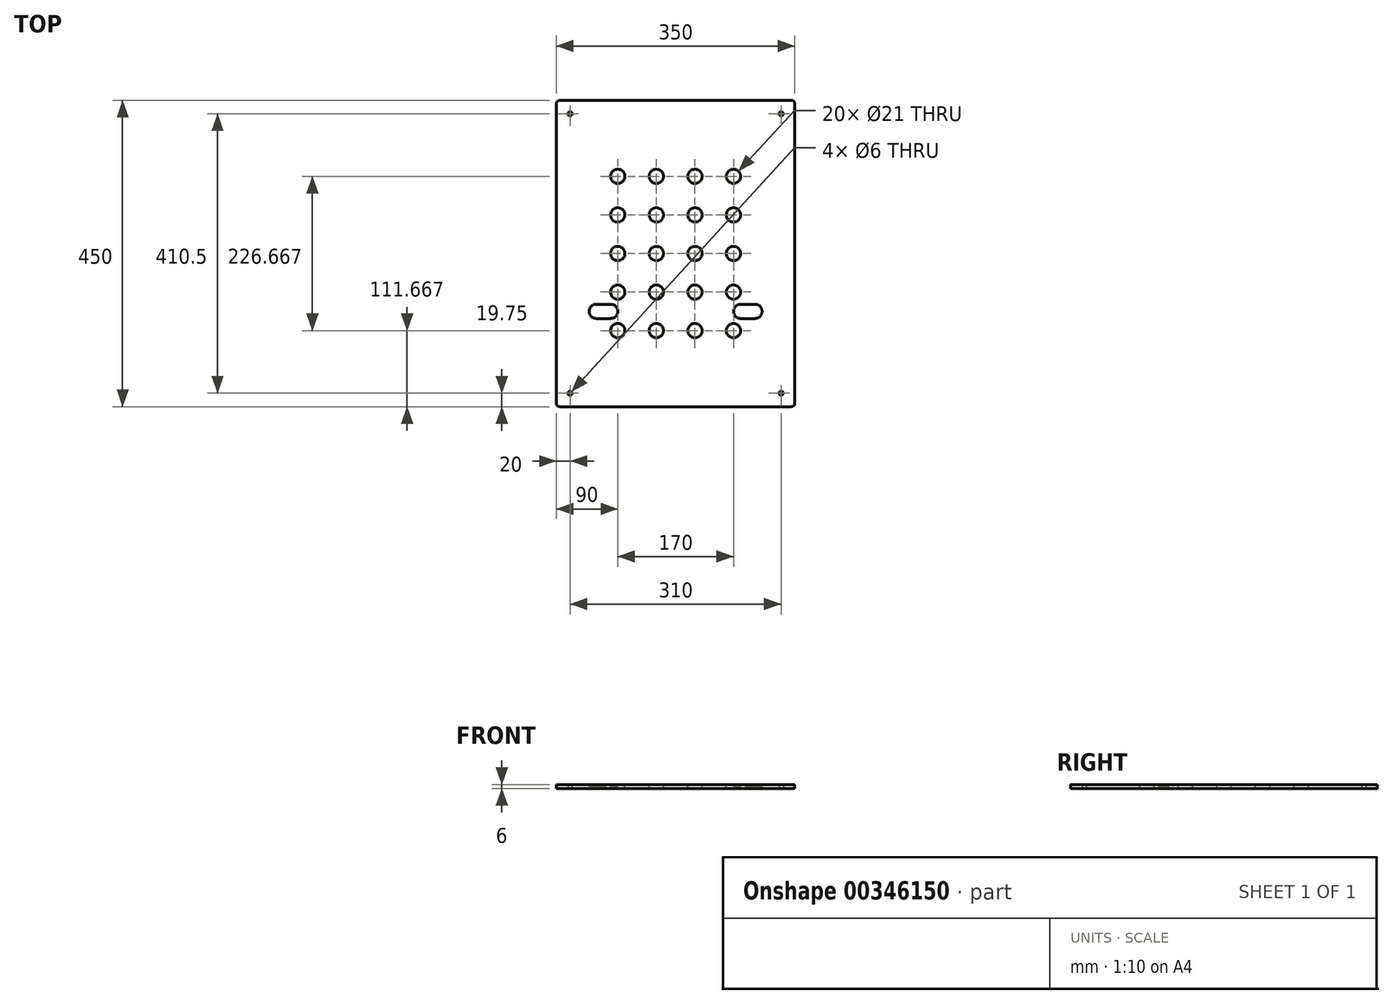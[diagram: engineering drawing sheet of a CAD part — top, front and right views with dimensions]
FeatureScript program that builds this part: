
annotation { "Feature Type Name" : "Feature", "Feature Type Description" : "" }
export const myFeature = defineFeature(function(context is Context, id is Id, definition is map)
    precondition{}
    {
        {
            var Q0;
            Q0=qCreatedBy(makeId("Top.planeOp"),FACE);
            var sketch = newSketch(context, id + "F0", { "sketchPlane" : qUnion([Q0])});
            skLineSegment(sketch, "E0.bottom", {"start": v(-170, 225) * mm, "end": v(170, 225) * mm});
            skLineSegment(sketch, "E0.top", {"start": v(-170, -225) * mm, "end": v(170, -225) * mm});
            skLineSegment(sketch, "E0.left", {"start": v(-175, 220) * mm, "end": v(-175, -220) * mm});
            skLineSegment(sketch, "E0.right", {"start": v(175, 220) * mm, "end": v(175, -220) * mm});
            skCircle(sketch, "E1", {"center": v(155, 205.25) * mm, "radius": 3 * mm});
            skCircle(sketch, "E2", {"center": v(155, -205.25) * mm, "radius": 3 * mm});
            skCircle(sketch, "E3", {"center": v(-155, -205.25) * mm, "radius": 3 * mm});
            skCircle(sketch, "E4", {"center": v(-155, 205.25) * mm, "radius": 3 * mm});
            skPoint(sketch, "E5.visualSharp", {"position": v(-175, 225) * mm});
            skArc(sketch, "E5.filletArc", {"start": v(-170, 225) * mm, "mid": v(-173.54, 223.54) * mm, "end": v(-175, 220) * mm});
            skPoint(sketch, "E6.visualSharp", {"position": v(-175, -225) * mm});
            skArc(sketch, "E6.filletArc", {"start": v(-175, -220) * mm, "mid": v(-173.54, -223.54) * mm, "end": v(-170, -225) * mm});
            skPoint(sketch, "E7.visualSharp", {"position": v(175, -225) * mm});
            skArc(sketch, "E7.filletArc", {"start": v(170, -225) * mm, "mid": v(173.54, -223.54) * mm, "end": v(175, -220) * mm});
            skPoint(sketch, "E8.visualSharp", {"position": v(175, 225) * mm});
            skArc(sketch, "E8.filletArc", {"start": v(175, 220) * mm, "mid": v(173.54, 223.54) * mm, "end": v(170, 225) * mm});
            skSolve(sketch);
        }
        {
            var Q0;
            Q0=makeQuery(id+"F0.imprint","IMPRINT",FACE,{"disambiguationData":[TD([[makeQuery(id+"F0.imprint","IMPRINT",EDGE,{"derivedFrom":sQuery(id+"F0.wireOp",EDGE,"E0.bottom")}),-1.0]])]});
            extrude(context, id + "F1", {"entities" : qUnion([Q0]), "depth" : 6 * mm});
        }
        {
            var Q0;
            Q0=makeQuery(id+"F1.opExtrude","CAP_FACE",FACE,{"disambiguationData":[OSD([sQuery(id+"F0.wireOp",EDGE,"E0.bottom"),sQuery(id+"F0.wireOp",EDGE,"E0.top"),sQuery(id+"F0.wireOp",EDGE,"E0.left"),sQuery(id+"F0.wireOp",EDGE,"E0.right"),sQuery(id+"F0.wireOp",EDGE,"E1"),sQuery(id+"F0.wireOp",EDGE,"E2"),sQuery(id+"F0.wireOp",EDGE,"E3"),sQuery(id+"F0.wireOp",EDGE,"E4"),sQuery(id+"F0.wireOp",EDGE,"E5.filletArc"),sQuery(id+"F0.wireOp",EDGE,"E6.filletArc"),sQuery(id+"F0.wireOp",EDGE,"E7.filletArc"),sQuery(id+"F0.wireOp",EDGE,"E8.filletArc")])],"isStart":false});
            var sketch = newSketch(context, id + "F2", { "sketchPlane" : qUnion([Q0])});
            skLineSegment(sketch, "E9.bottom", {"start": v(-125, 145) * mm, "end": v(125, 145) * mm, "construction": true});
            skLineSegment(sketch, "E9.top", {"start": v(-125, -145) * mm, "end": v(125, -145) * mm, "construction": true});
            skLineSegment(sketch, "E9.left", {"start": v(-125, 145) * mm, "end": v(-125, -145) * mm, "construction": true});
            skLineSegment(sketch, "E9.right", {"start": v(125, 145) * mm, "end": v(125, -145) * mm, "construction": true});
            skCircle(sketch, "E10", {"center": v(-85, 113.33) * mm, "radius": 10.5 * mm});
            skCircle(sketch, "E11.0.1.0", {"center": v(-85, 56.67) * mm, "radius": 10.5 * mm});
            skCircle(sketch, "E11.0.2.0", {"center": v(-85, 0) * mm, "radius": 10.5 * mm});
            skCircle(sketch, "E11.1.0.0", {"center": v(-28.33, 113.33) * mm, "radius": 10.5 * mm});
            skCircle(sketch, "E11.1.1.0", {"center": v(-28.33, 56.67) * mm, "radius": 10.5 * mm});
            skCircle(sketch, "E11.1.2.0", {"center": v(-28.33, 0) * mm, "radius": 10.5 * mm});
            skCircle(sketch, "E11.2.0.0", {"center": v(28.33, 113.33) * mm, "radius": 10.5 * mm});
            skCircle(sketch, "E11.2.1.0", {"center": v(28.33, 56.67) * mm, "radius": 10.5 * mm});
            skCircle(sketch, "E11.2.2.0", {"center": v(28.33, 0) * mm, "radius": 10.5 * mm});
            skLineSegment(sketch, "E11.direction1", {"start": v(-85, 113.33) * mm, "end": v(-28.33, 113.33) * mm, "construction": true});
            skLineSegment(sketch, "E11.direction2", {"start": v(-85, 113.33) * mm, "end": v(-85, 56.67) * mm, "construction": true});
            skCircle(sketch, "E12.0.0.3", {"center": v(-85, -56.67) * mm, "radius": 10.5 * mm});
            skCircle(sketch, "E12.0.0.4", {"center": v(-85, -113.33) * mm, "radius": 10.5 * mm});
            skCircle(sketch, "E12.0.1.3", {"center": v(-28.33, -56.67) * mm, "radius": 10.5 * mm});
            skCircle(sketch, "E12.0.1.4", {"center": v(-28.33, -113.33) * mm, "radius": 10.5 * mm});
            skCircle(sketch, "E12.0.2.3", {"center": v(28.33, -56.67) * mm, "radius": 10.5 * mm});
            skCircle(sketch, "E12.0.2.4", {"center": v(28.33, -113.33) * mm, "radius": 10.5 * mm});
            skCircle(sketch, "E13.0.3.0", {"center": v(85, 113.33) * mm, "radius": 10.5 * mm});
            skCircle(sketch, "E13.0.3.1", {"center": v(85, 56.67) * mm, "radius": 10.5 * mm});
            skCircle(sketch, "E13.0.3.2", {"center": v(85, 0) * mm, "radius": 10.5 * mm});
            skCircle(sketch, "E13.0.3.3", {"center": v(85, -56.67) * mm, "radius": 10.5 * mm});
            skCircle(sketch, "E13.0.3.4", {"center": v(85, -113.33) * mm, "radius": 10.5 * mm});
            skSolve(sketch);
        }
        {
            var Q0;
            Q0=makeQuery(id+"F2.imprint","IMPRINT",FACE,{"disambiguationData":[TD([[makeQuery(id+"F2.imprint","IMPRINT",EDGE,{"derivedFrom":sQuery(id+"F2.wireOp",EDGE,"E10")}),1.0]])]});
            var Q1;
            Q1=makeQuery(id+"F2.imprint","IMPRINT",FACE,{"disambiguationData":[TD([[makeQuery(id+"F2.imprint","IMPRINT",EDGE,{"derivedFrom":sQuery(id+"F2.wireOp",EDGE,"E11.0.1.0")}),1.0]])]});
            var Q2;
            Q2=makeQuery(id+"F2.imprint","IMPRINT",FACE,{"disambiguationData":[TD([[makeQuery(id+"F2.imprint","IMPRINT",EDGE,{"derivedFrom":sQuery(id+"F2.wireOp",EDGE,"E11.0.2.0")}),1.0]])]});
            var Q3;
            Q3=makeQuery(id+"F2.imprint","IMPRINT",FACE,{"disambiguationData":[TD([[makeQuery(id+"F2.imprint","IMPRINT",EDGE,{"derivedFrom":sQuery(id+"F2.wireOp",EDGE,"E12.0.0.3")}),1.0]])]});
            var Q4;
            Q4=makeQuery(id+"F2.imprint","IMPRINT",FACE,{"disambiguationData":[TD([[makeQuery(id+"F2.imprint","IMPRINT",EDGE,{"derivedFrom":sQuery(id+"F2.wireOp",EDGE,"E12.0.0.4")}),1.0]])]});
            var Q5;
            Q5=makeQuery(id+"F2.imprint","IMPRINT",FACE,{"disambiguationData":[TD([[makeQuery(id+"F2.imprint","IMPRINT",EDGE,{"derivedFrom":sQuery(id+"F2.wireOp",EDGE,"E12.0.1.4")}),1.0]])]});
            var Q6;
            Q6=makeQuery(id+"F2.imprint","IMPRINT",FACE,{"disambiguationData":[TD([[makeQuery(id+"F2.imprint","IMPRINT",EDGE,{"derivedFrom":sQuery(id+"F2.wireOp",EDGE,"E12.0.1.3")}),1.0]])]});
            var Q7;
            Q7=makeQuery(id+"F2.imprint","IMPRINT",FACE,{"disambiguationData":[TD([[makeQuery(id+"F2.imprint","IMPRINT",EDGE,{"derivedFrom":sQuery(id+"F2.wireOp",EDGE,"E11.1.2.0")}),1.0]])]});
            var Q8;
            Q8=makeQuery(id+"F2.imprint","IMPRINT",FACE,{"disambiguationData":[TD([[makeQuery(id+"F2.imprint","IMPRINT",EDGE,{"derivedFrom":sQuery(id+"F2.wireOp",EDGE,"E11.1.1.0")}),1.0]])]});
            var Q9;
            Q9=makeQuery(id+"F2.imprint","IMPRINT",FACE,{"disambiguationData":[TD([[makeQuery(id+"F2.imprint","IMPRINT",EDGE,{"derivedFrom":sQuery(id+"F2.wireOp",EDGE,"E11.1.0.0")}),1.0]])]});
            var Q10;
            Q10=makeQuery(id+"F2.imprint","IMPRINT",FACE,{"disambiguationData":[TD([[makeQuery(id+"F2.imprint","IMPRINT",EDGE,{"derivedFrom":sQuery(id+"F2.wireOp",EDGE,"E11.2.0.0")}),1.0]])]});
            var Q11;
            Q11=makeQuery(id+"F2.imprint","IMPRINT",FACE,{"disambiguationData":[TD([[makeQuery(id+"F2.imprint","IMPRINT",EDGE,{"derivedFrom":sQuery(id+"F2.wireOp",EDGE,"E11.2.1.0")}),1.0]])]});
            var Q12;
            Q12=makeQuery(id+"F2.imprint","IMPRINT",FACE,{"disambiguationData":[TD([[makeQuery(id+"F2.imprint","IMPRINT",EDGE,{"derivedFrom":sQuery(id+"F2.wireOp",EDGE,"E11.2.2.0")}),1.0]])]});
            var Q13;
            Q13=makeQuery(id+"F2.imprint","IMPRINT",FACE,{"disambiguationData":[TD([[makeQuery(id+"F2.imprint","IMPRINT",EDGE,{"derivedFrom":sQuery(id+"F2.wireOp",EDGE,"E12.0.2.3")}),1.0]])]});
            var Q14;
            Q14=makeQuery(id+"F2.imprint","IMPRINT",FACE,{"disambiguationData":[TD([[makeQuery(id+"F2.imprint","IMPRINT",EDGE,{"derivedFrom":sQuery(id+"F2.wireOp",EDGE,"E12.0.2.4")}),1.0]])]});
            var Q15;
            Q15=makeQuery(id+"F2.imprint","IMPRINT",FACE,{"disambiguationData":[TD([[makeQuery(id+"F2.imprint","IMPRINT",EDGE,{"derivedFrom":sQuery(id+"F2.wireOp",EDGE,"E13.0.3.4")}),1.0]])]});
            var Q16;
            Q16=makeQuery(id+"F2.imprint","IMPRINT",FACE,{"disambiguationData":[TD([[makeQuery(id+"F2.imprint","IMPRINT",EDGE,{"derivedFrom":sQuery(id+"F2.wireOp",EDGE,"E13.0.3.3")}),1.0]])]});
            var Q17;
            Q17=makeQuery(id+"F2.imprint","IMPRINT",FACE,{"disambiguationData":[TD([[makeQuery(id+"F2.imprint","IMPRINT",EDGE,{"derivedFrom":sQuery(id+"F2.wireOp",EDGE,"E13.0.3.2")}),1.0]])]});
            var Q18;
            Q18=makeQuery(id+"F2.imprint","IMPRINT",FACE,{"disambiguationData":[TD([[makeQuery(id+"F2.imprint","IMPRINT",EDGE,{"derivedFrom":sQuery(id+"F2.wireOp",EDGE,"E13.0.3.1")}),1.0]])]});
            var Q19;
            Q19=makeQuery(id+"F2.imprint","IMPRINT",FACE,{"disambiguationData":[TD([[makeQuery(id+"F2.imprint","IMPRINT",EDGE,{"derivedFrom":sQuery(id+"F2.wireOp",EDGE,"E13.0.3.0")}),1.0]])]});
            extrude(context, id + "F3", {"entities" : qUnion([Q0, Q1, Q2, Q3, Q4, Q5, Q6, Q7, Q8, Q9, Q10, Q11, Q12, Q13, Q14, Q15, Q16, Q17, Q18, Q19]), "operationType" : NewBodyOperationType.REMOVE, "oppositeDirection" : true, "depth" : 25 * mm});
        }
        {
            var Q0;
            Q0=makeQuery(id+"F1.opExtrude","CAP_FACE",FACE,{"disambiguationData":[OSD([sQuery(id+"F0.wireOp",EDGE,"E0.bottom"),sQuery(id+"F0.wireOp",EDGE,"E0.top"),sQuery(id+"F0.wireOp",EDGE,"E0.left"),sQuery(id+"F0.wireOp",EDGE,"E0.right"),sQuery(id+"F0.wireOp",EDGE,"E1"),sQuery(id+"F0.wireOp",EDGE,"E2"),sQuery(id+"F0.wireOp",EDGE,"E3"),sQuery(id+"F0.wireOp",EDGE,"E4"),sQuery(id+"F0.wireOp",EDGE,"E5.filletArc"),sQuery(id+"F0.wireOp",EDGE,"E6.filletArc"),sQuery(id+"F0.wireOp",EDGE,"E7.filletArc"),sQuery(id+"F0.wireOp",EDGE,"E8.filletArc")])],"isStart":false});
            var sketch = newSketch(context, id + "F4", { "sketchPlane" : qUnion([Q0])});
            skPoint(sketch, "E14.startSnap0", {"position": v(-85, 28.33) * mm});
            skLineSegment(sketch, "E15", {"start": v(-85, -56.67) * mm, "end": v(-85, -113.33) * mm, "construction": true});
            skLineSegment(sketch, "E16", {"start": v(85, -56.67) * mm, "end": v(85, -113.33) * mm, "construction": true});
            skLineSegment(sketch, "E17", {"start": v(85, -85) * mm, "end": v(-85, -85) * mm, "construction": true});
            skLineSegment(sketch, "E18.bottom", {"start": v(-116.5, -74.5) * mm, "end": v(-95.5, -74.5) * mm});
            skLineSegment(sketch, "E18.top", {"start": v(-116.5, -95.5) * mm, "end": v(-95.5, -95.5) * mm});
            skLineSegment(sketch, "E18.left", {"start": v(-116.5, -74.5) * mm, "end": v(-116.5, -95.5) * mm, "construction": true});
            skLineSegment(sketch, "E18.right", {"start": v(-95.5, -74.5) * mm, "end": v(-95.5, -95.5) * mm, "construction": true});
            skArc(sketch, "E19", {"start": v(-95.5, -95.5) * mm, "mid": v(-85, -85) * mm, "end": v(-95.5, -74.5) * mm});
            skArc(sketch, "E20", {"start": v(-116.5, -74.5) * mm, "mid": v(-127, -85) * mm, "end": v(-116.5, -95.5) * mm});
            skLineSegment(sketch, "E21", {"start": v(0, 10.87) * mm, "end": v(0, -151.01) * mm, "construction": true});
            skLineSegment(sketch, "E22.MirrorCS", {"start": v(116.5, -74.5) * mm, "end": v(95.5, -74.5) * mm});
            skArc(sketch, "E23.MirrorCS", {"start": v(95.5, -95.5) * mm, "mid": v(85, -85) * mm, "end": v(95.5, -74.5) * mm});
            skLineSegment(sketch, "E24.MirrorCS", {"start": v(116.5, -95.5) * mm, "end": v(95.5, -95.5) * mm});
            skArc(sketch, "E25.MirrorCS", {"start": v(116.5, -74.5) * mm, "mid": v(127, -85) * mm, "end": v(116.5, -95.5) * mm});
            skSolve(sketch);
        }
        {
            var Q0;
            Q0=makeQuery(id+"F4.imprint","IMPRINT",FACE,{"disambiguationData":[TD([[makeQuery(id+"F4.imprint","IMPRINT",EDGE,{"derivedFrom":sQuery(id+"F4.wireOp",EDGE,"E18.bottom")}),-1.0]])]});
            var Q1;
            Q1=makeQuery(id+"F4.imprint","IMPRINT",FACE,{"disambiguationData":[TD([[makeQuery(id+"F4.imprint","IMPRINT",EDGE,{"derivedFrom":sQuery(id+"F4.wireOp",EDGE,"E22.MirrorCS")}),1.0]])]});
            extrude(context, id + "F5", {"entities" : qUnion([Q0, Q1]), "operationType" : NewBodyOperationType.REMOVE, "oppositeDirection" : true, "depth" : 3 * mm});
        }
    });
